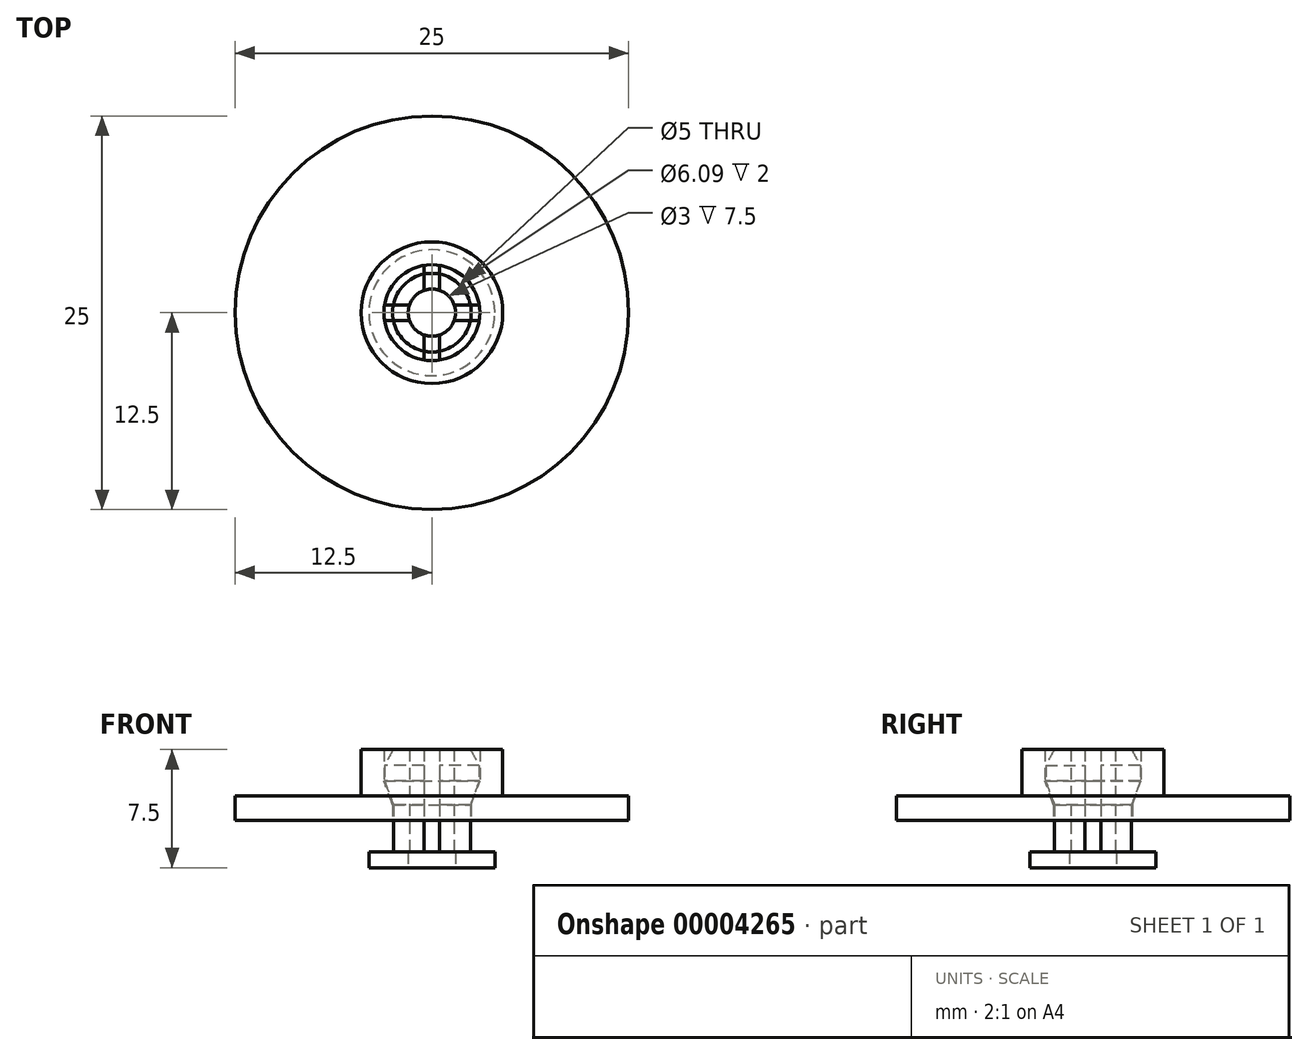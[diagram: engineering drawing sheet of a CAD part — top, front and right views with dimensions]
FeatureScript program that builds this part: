
annotation { "Feature Type Name" : "Feature", "Feature Type Description" : "" }
export const myFeature = defineFeature(function(context is Context, id is Id, definition is map)
    precondition{}
    {
        {
            var Q0;
            Q0=qCreatedBy(makeId("Front.planeOp"),FACE);
            var sketch = newSketch(context, id + "F0", { "sketchPlane" : qUnion([Q0])});
            skLineSegment(sketch, "E0", {"start": v(-8.26, 0) * mm, "end": v(0, 0) * mm, "construction": true});
            skLineSegment(sketch, "E1", {"start": v(0, 0) * mm, "end": v(0, 12.35) * mm, "construction": true});
            skLineSegment(sketch, "E2", {"start": v(-1.5, 0) * mm, "end": v(-4, 0) * mm});
            skLineSegment(sketch, "E3", {"start": v(-4, 0) * mm, "end": v(-4, 1) * mm});
            skLineSegment(sketch, "E4", {"start": v(-4, 1) * mm, "end": v(-2.5, 1) * mm});
            skLineSegment(sketch, "E5", {"start": v(-2.5, 1) * mm, "end": v(-2.5, 4) * mm});
            skLineSegment(sketch, "E6", {"start": v(-2.5, 4) * mm, "end": v(-3.05, 5.5) * mm});
            skLineSegment(sketch, "E7", {"start": v(-3.05, 5.5) * mm, "end": v(-3.05, 6.5) * mm});
            skLineSegment(sketch, "E8", {"start": v(-3.05, 6.5) * mm, "end": v(-2.5, 7.5) * mm});
            skLineSegment(sketch, "E9", {"start": v(-1.5, 0) * mm, "end": v(-1.5, 7.5) * mm});
            skLineSegment(sketch, "E10", {"start": v(-1.5, 7.5) * mm, "end": v(-2.5, 7.5) * mm});
            skLineSegment(sketch, "E11", {"start": v(0, 0) * mm, "end": v(8.26, 0) * mm, "construction": true});
            skLineSegment(sketch, "E12", {"start": v(-2.5, 3) * mm, "end": v(-12.5, 3) * mm});
            skLineSegment(sketch, "E13", {"start": v(-4.5, 7.5) * mm, "end": v(-3.05, 7.5) * mm});
            skLineSegment(sketch, "E14", {"start": v(-3.05, 7.5) * mm, "end": v(-3.05, 6.5) * mm});
            skLineSegment(sketch, "E15", {"start": v(-4.5, 7.5) * mm, "end": v(-4.5, 4.57) * mm});
            skLineSegment(sketch, "E16", {"start": v(-4.5, 4.57) * mm, "end": v(-12.5, 4.57) * mm});
            skLineSegment(sketch, "E17", {"start": v(-12.5, 4.57) * mm, "end": v(-12.5, 3) * mm});
            skSolve(sketch);
        }
        {
            var Q0;
            Q0=makeQuery(id+"F0.imprint","IMPRINT",FACE,{"disambiguationData":[TD([[makeQuery(id+"F0.imprint","IMPRINT",EDGE,{"derivedFrom":sQuery(id+"F0.wireOp",EDGE,"E2")}),-1.0]])]});
            var Q1;
            Q1=sQuery(id+"F0.wireOp",EDGE,"E1");
            revolve(context, id + "F1", {"entities" : qUnion([Q0]), "axis" : qUnion([Q1]), "revolveType" : RevolveType.FULL});
        }
        {
            var Q0;
            Q0=makeQuery(id+"F1.opRevolve","SWEPT_FACE",FACE,{"disambiguationData":[OSD([sQuery(id+"F0.wireOp",EDGE,"E4")])]});
            var sketch = newSketch(context, id + "F2", { "sketchPlane" : qUnion([Q0])});
            skLineSegment(sketch, "E18", {"start": v(-4, 0) * mm, "end": v(-4, 0.5) * mm});
            skLineSegment(sketch, "E19", {"start": v(-4, 0.5) * mm, "end": v(-0.5, 0.5) * mm});
            skLineSegment(sketch, "E20", {"start": v(0, 4) * mm, "end": v(-0.5, 4) * mm});
            skLineSegment(sketch, "E21", {"start": v(-0.5, 4) * mm, "end": v(-0.5, 0.5) * mm});
            skLineSegment(sketch, "E22.1.0", {"start": v(-4, -0.5) * mm, "end": v(-0.5, -0.5) * mm});
            skLineSegment(sketch, "E22.1.1", {"start": v(-4, 0) * mm, "end": v(-4, -0.5) * mm});
            skLineSegment(sketch, "E22.1.2", {"start": v(-0.5, -4) * mm, "end": v(-0.5, -0.5) * mm});
            skLineSegment(sketch, "E22.1.3", {"start": v(0, -4) * mm, "end": v(-0.5, -4) * mm});
            skLineSegment(sketch, "E22.2.0", {"start": v(0.5, -4) * mm, "end": v(0.5, -0.5) * mm});
            skLineSegment(sketch, "E22.2.1", {"start": v(0, -4) * mm, "end": v(0.5, -4) * mm});
            skLineSegment(sketch, "E22.2.2", {"start": v(4, -0.5) * mm, "end": v(0.5, -0.5) * mm});
            skLineSegment(sketch, "E22.2.3", {"start": v(4, 0) * mm, "end": v(4, -0.5) * mm});
            skLineSegment(sketch, "E22.3.0", {"start": v(4, 0.5) * mm, "end": v(0.5, 0.5) * mm});
            skLineSegment(sketch, "E22.3.1", {"start": v(4, 0) * mm, "end": v(4, 0.5) * mm});
            skLineSegment(sketch, "E22.3.2", {"start": v(0.5, 4) * mm, "end": v(0.5, 0.5) * mm});
            skLineSegment(sketch, "E22.3.3", {"start": v(0, 4) * mm, "end": v(0.5, 4) * mm});
            skPoint(sketch, "E22.center", {"position": v(0, 0) * mm});
            skSolve(sketch);
        }
        {
            var Q0;
            {var subQ3=sQuery(id+"F2.wireOp",EDGE,"E21");var subQ11=sQuery(id+"F2.wireOp",EDGE,"E19");var subQ20=makeQuery(id+"F2.imprint","INTERSECT",VERTEX,{"derivedFrom":[subQ11,subQ3]});Q0=makeQuery(id+"F2.imprint","IMPRINT",FACE,{"disambiguationData":[TD([[makeQuery(id+"F2.imprint","IMPRINT",EDGE,{"disambiguationData":[TD([[subQ20,1.0]])],"derivedFrom":subQ11}),-1.0]])]});}
            var Q1;
            {var subQ0=sQuery(id+"F0.wireOp",EDGE,"E4");var subQ1=makeQuery(id+"F1.opRevolve","SWEPT_EDGE",EDGE,{"disambiguationData":[OSD([sQuery(id+"F0.wireOp",EDGE,"E3"),subQ0])]});var subQ5=sQuery(id+"F2.wireOp",EDGE,"E19");var subQ6=makeQuery(id+"F2.imprint","INTERSECT",VERTEX,{"derivedFrom":[subQ1,subQ5]});Q1=makeQuery(id+"F2.imprint","IMPRINT",FACE,{"disambiguationData":[TD([[makeQuery(id+"F2.imprint","IMPRINT",EDGE,{"disambiguationData":[TD([[subQ6,-1.0]])],"derivedFrom":subQ5}),-1.0]])]});}
            var Q2;
            {var subQ0=sQuery(id+"F0.wireOp",EDGE,"E4");var subQ4=sQuery(id+"F2.wireOp",EDGE,"E21");var subQ6=makeQuery(id+"F1.opRevolve","SWEPT_EDGE",EDGE,{"disambiguationData":[OSD([sQuery(id+"F0.wireOp",EDGE,"E3"),subQ0])]});var subQ9=makeQuery(id+"F2.imprint","INTERSECT",VERTEX,{"derivedFrom":[subQ6,subQ4]});Q2=makeQuery(id+"F2.imprint","IMPRINT",FACE,{"disambiguationData":[TD([[makeQuery(id+"F2.imprint","IMPRINT",EDGE,{"disambiguationData":[TD([[subQ9,-1.0]])],"derivedFrom":subQ4}),1.0]])]});}
            var Q3;
            {var subQ0=sQuery(id+"F0.wireOp",EDGE,"E4");var subQ4=sQuery(id+"F2.wireOp",EDGE,"E22.2.2");var subQ6=makeQuery(id+"F1.opRevolve","SWEPT_EDGE",EDGE,{"disambiguationData":[OSD([sQuery(id+"F0.wireOp",EDGE,"E3"),subQ0])]});var subQ9=makeQuery(id+"F2.imprint","INTERSECT",VERTEX,{"derivedFrom":[subQ6,subQ4]});Q3=makeQuery(id+"F2.imprint","IMPRINT",FACE,{"disambiguationData":[TD([[makeQuery(id+"F2.imprint","IMPRINT",EDGE,{"disambiguationData":[TD([[subQ9,-1.0]])],"derivedFrom":subQ4}),-1.0]])]});}
            var Q4;
            {var subQ0=sQuery(id+"F0.wireOp",EDGE,"E4");var subQ1=makeQuery(id+"F1.opRevolve","SWEPT_EDGE",EDGE,{"disambiguationData":[OSD([sQuery(id+"F0.wireOp",EDGE,"E3"),subQ0])]});var subQ7=sQuery(id+"F2.wireOp",EDGE,"E22.1.2");var subQ9=makeQuery(id+"F2.imprint","INTERSECT",VERTEX,{"derivedFrom":[subQ1,subQ7]});Q4=makeQuery(id+"F2.imprint","IMPRINT",FACE,{"disambiguationData":[TD([[makeQuery(id+"F2.imprint","IMPRINT",EDGE,{"disambiguationData":[TD([[subQ9,-1.0]])],"derivedFrom":subQ7}),-1.0]])]});}
            var Q5;
            Q5=makeQuery(id+"F1.opRevolve","SWEPT_FACE",FACE,{"disambiguationData":[OSD([sQuery(id+"F0.wireOp",EDGE,"E10")])]});
            extrude(context, id + "F3", {"entities" : qUnion([Q0, Q1, Q2, Q3, Q4]), "operationType" : NewBodyOperationType.REMOVE, "endBound" : BoundingType.UP_TO_SURFACE, "endBoundEntityFace" : qUnion([Q5]), "depth" : 25 * mm});
        }
        {
            var Q0;
            {var subQ1=sQuery(id+"F0.wireOp",EDGE,"E6");Q0=makeQuery(id+"F0.imprint","IMPRINT",FACE,{"disambiguationData":[TD([[makeQuery(id+"F0.imprint","IMPRINT",EDGE,{"derivedFrom":subQ1}),1.0]])]});}
            var Q1;
            Q1=sQuery(id+"F0.wireOp",EDGE,"E1");
            revolve(context, id + "F4", {"entities" : qUnion([Q0]), "axis" : qUnion([Q1]), "revolveType" : RevolveType.FULL});
        }
    });
